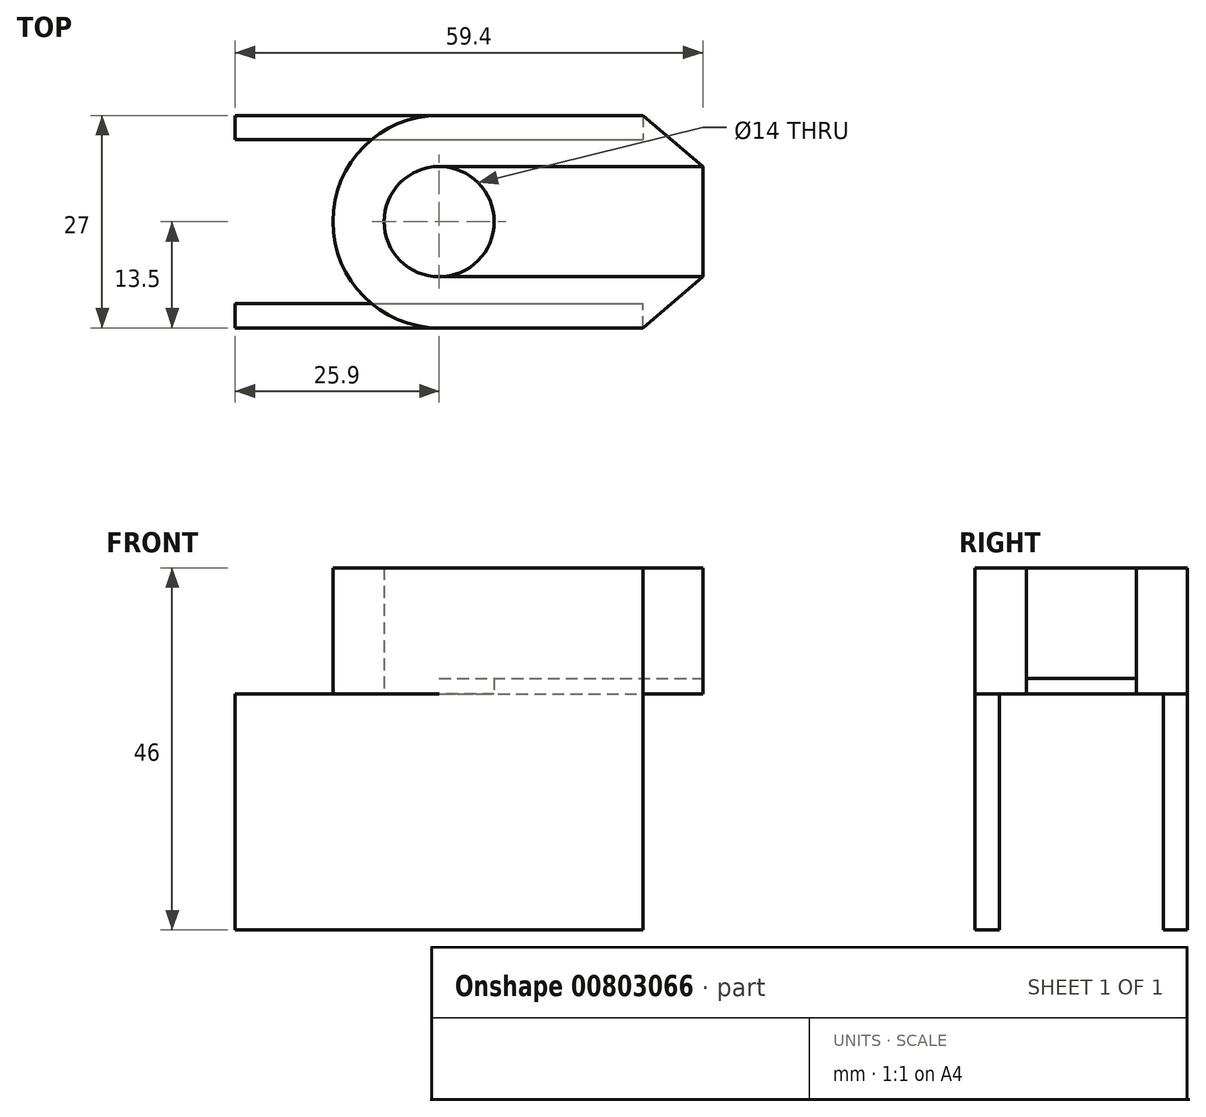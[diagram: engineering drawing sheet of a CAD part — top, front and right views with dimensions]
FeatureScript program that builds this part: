
annotation { "Feature Type Name" : "Feature", "Feature Type Description" : "" }
export const myFeature = defineFeature(function(context is Context, id is Id, definition is map)
    precondition{}
    {
        {
            var Q0;
            Q0=qCreatedBy(makeId("Top.planeOp"),FACE);
            var sketch = newSketch(context, id + "F0", { "sketchPlane" : qUnion([Q0])});
            skLineSegment(sketch, "E0.bottom", {"start": v(-33.5, 13.5) * mm, "end": v(33.5, 13.5) * mm});
            skLineSegment(sketch, "E0.top", {"start": v(-33.5, -13.5) * mm, "end": v(33.5, -13.5) * mm});
            skLineSegment(sketch, "E0.left", {"start": v(-33.5, 13.5) * mm, "end": v(-33.5, -13.5) * mm});
            skLineSegment(sketch, "E0.right", {"start": v(33.5, 13.5) * mm, "end": v(33.5, -13.5) * mm});
            skPoint(sketch, "E0.middle", {"position": v(0, 0) * mm});
            skCircle(sketch, "E1", {"center": v(0, 0) * mm, "radius": 7 * mm});
            skCircle(sketch, "E2", {"center": v(0, 0) * mm, "radius": 13.5 * mm});
            skLineSegment(sketch, "E3", {"start": v(0, 7) * mm, "end": v(33.5, 7) * mm});
            skLineSegment(sketch, "E4", {"start": v(0, -7) * mm, "end": v(33.5, -7) * mm});
            skLineSegment(sketch, "E5", {"start": v(-33.5, 7) * mm, "end": v(-33.5, -7) * mm});
            skPoint(sketch, "E5.startSnap0", {"position": v(16.75, 7) * mm});
            skLineSegment(sketch, "E6", {"start": v(-33.5, 7) * mm, "end": v(-25.9, 13.5) * mm});
            skLineSegment(sketch, "E7.MirrorCS", {"start": v(-33.5, -7) * mm, "end": v(-25.9, -13.5) * mm});
            skLineSegment(sketch, "E8.MirrorCS", {"start": v(33.5, 7) * mm, "end": v(25.9, 13.5) * mm});
            skLineSegment(sketch, "E9.MirrorCS", {"start": v(33.5, -7) * mm, "end": v(25.9, -13.5) * mm});
            skSolve(sketch);
        }
        {
            var Q0;
            {var subQ5=sQuery(id+"F0.wireOp",EDGE,"E3");var subQ7=sQuery(id+"F0.wireOp",EDGE,"E1");var subQ8=makeQuery(id+"F0.imprint","INTERSECT",VERTEX,{"derivedFrom":[subQ7,subQ5]});Q0=makeQuery(id+"F0.imprint","IMPRINT",FACE,{"disambiguationData":[TD([[makeQuery(id+"F0.imprint","IMPRINT",EDGE,{"disambiguationData":[TD([[subQ8,-1.0]])],"derivedFrom":subQ7}),-1.0]])]});}
            var Q1;
            {var subQ0=sQuery(id+"F0.wireOp",EDGE,"E9.MirrorCS");Q1=makeQuery(id+"F0.imprint","IMPRINT",FACE,{"disambiguationData":[TD([[makeQuery(id+"F0.imprint","IMPRINT",EDGE,{"derivedFrom":subQ0}),-1.0]])]});}
            var Q2;
            {var subQ0=sQuery(id+"F0.wireOp",EDGE,"E8.MirrorCS");Q2=makeQuery(id+"F0.imprint","IMPRINT",FACE,{"disambiguationData":[TD([[makeQuery(id+"F0.imprint","IMPRINT",EDGE,{"derivedFrom":subQ0}),1.0]])]});}
            extrude(context, id + "F1", {"entities" : qUnion([Q0, Q1, Q2]), "depth" : 16 * mm, "offsetDistance" : 25 * mm});
        }
        {
            var Q0;
            Q0=qCreatedBy(makeId("Top.planeOp"),FACE);
            var sketch = newSketch(context, id + "F2", { "sketchPlane" : qUnion([Q0])});
            skLineSegment(sketch, "E10.bottom", {"start": v(-25.9, -13.5) * mm, "end": v(25.9, -13.5) * mm});
            skLineSegment(sketch, "E10.top", {"start": v(-25.9, -10.4) * mm, "end": v(25.9, -10.4) * mm});
            skLineSegment(sketch, "E10.left", {"start": v(-25.9, -13.5) * mm, "end": v(-25.9, -10.4) * mm});
            skLineSegment(sketch, "E10.right", {"start": v(25.9, -13.5) * mm, "end": v(25.9, -10.4) * mm});
            skLineSegment(sketch, "E11.MirrorCS", {"start": v(-25.9, 10.4) * mm, "end": v(25.9, 10.4) * mm});
            skLineSegment(sketch, "E12.MirrorCS", {"start": v(-25.9, 13.5) * mm, "end": v(25.9, 13.5) * mm});
            skLineSegment(sketch, "E13.MirrorCS", {"start": v(25.9, 13.5) * mm, "end": v(25.9, 10.4) * mm});
            skLineSegment(sketch, "E14.MirrorCS", {"start": v(-25.9, 13.5) * mm, "end": v(-25.9, 10.4) * mm});
            skSolve(sketch);
        }
        {
            var Q0;
            Q0=makeQuery(id+"F2.imprint","IMPRINT",FACE,{"disambiguationData":[TD([[makeQuery(id+"F2.imprint","IMPRINT",EDGE,{"derivedFrom":sQuery(id+"F2.wireOp",EDGE,"E10.bottom")}),1.0]])]});
            var Q1;
            Q1=makeQuery(id+"F2.imprint","IMPRINT",FACE,{"disambiguationData":[TD([[makeQuery(id+"F2.imprint","IMPRINT",EDGE,{"derivedFrom":sQuery(id+"F2.wireOp",EDGE,"E11.MirrorCS")}),1.0]])]});
            extrude(context, id + "F3", {"entities" : qUnion([Q0, Q1]), "operationType" : NewBodyOperationType.ADD, "oppositeDirection" : true, "depth" : 30 * mm, "offsetDistance" : 25 * mm});
        }
        {
            var Q0;
            Q0=makeQuery(id+"F0.imprint","IMPRINT",FACE,{"disambiguationData":[TD([[makeQuery(id+"F0.imprint","IMPRINT",EDGE,{"derivedFrom":sQuery(id+"F0.wireOp",EDGE,"E5")}),1.0]])]});
            var Q1;
            {var subQ0=sQuery(id+"F0.wireOp",EDGE,"E3");var subQ5=sQuery(id+"F0.wireOp",EDGE,"E2");var subQ6=makeQuery(id+"F0.imprint","INTERSECT",VERTEX,{"derivedFrom":[subQ5,subQ0]});Q1=makeQuery(id+"F0.imprint","IMPRINT",FACE,{"disambiguationData":[TD([[makeQuery(id+"F0.imprint","IMPRINT",EDGE,{"disambiguationData":[TD([[subQ6,1.0]])],"derivedFrom":subQ5}),-1.0]])]});}
            var Q2;
            {var subQ0=sQuery(id+"F0.wireOp",EDGE,"E3");var subQ1=sQuery(id+"F0.wireOp",EDGE,"E1");var subQ2=makeQuery(id+"F0.imprint","INTERSECT",VERTEX,{"derivedFrom":[subQ1,subQ0]});Q2=makeQuery(id+"F0.imprint","IMPRINT",FACE,{"disambiguationData":[TD([[makeQuery(id+"F0.imprint","IMPRINT",EDGE,{"disambiguationData":[TD([[subQ2,1.0]])],"derivedFrom":subQ1}),-1.0]])]});}
            extrude(context, id + "F4", {"entities" : qUnion([Q0, Q1, Q2]), "operationType" : NewBodyOperationType.ADD, "depth" : 2 * mm, "offsetDistance" : 25 * mm});
        }
    });
